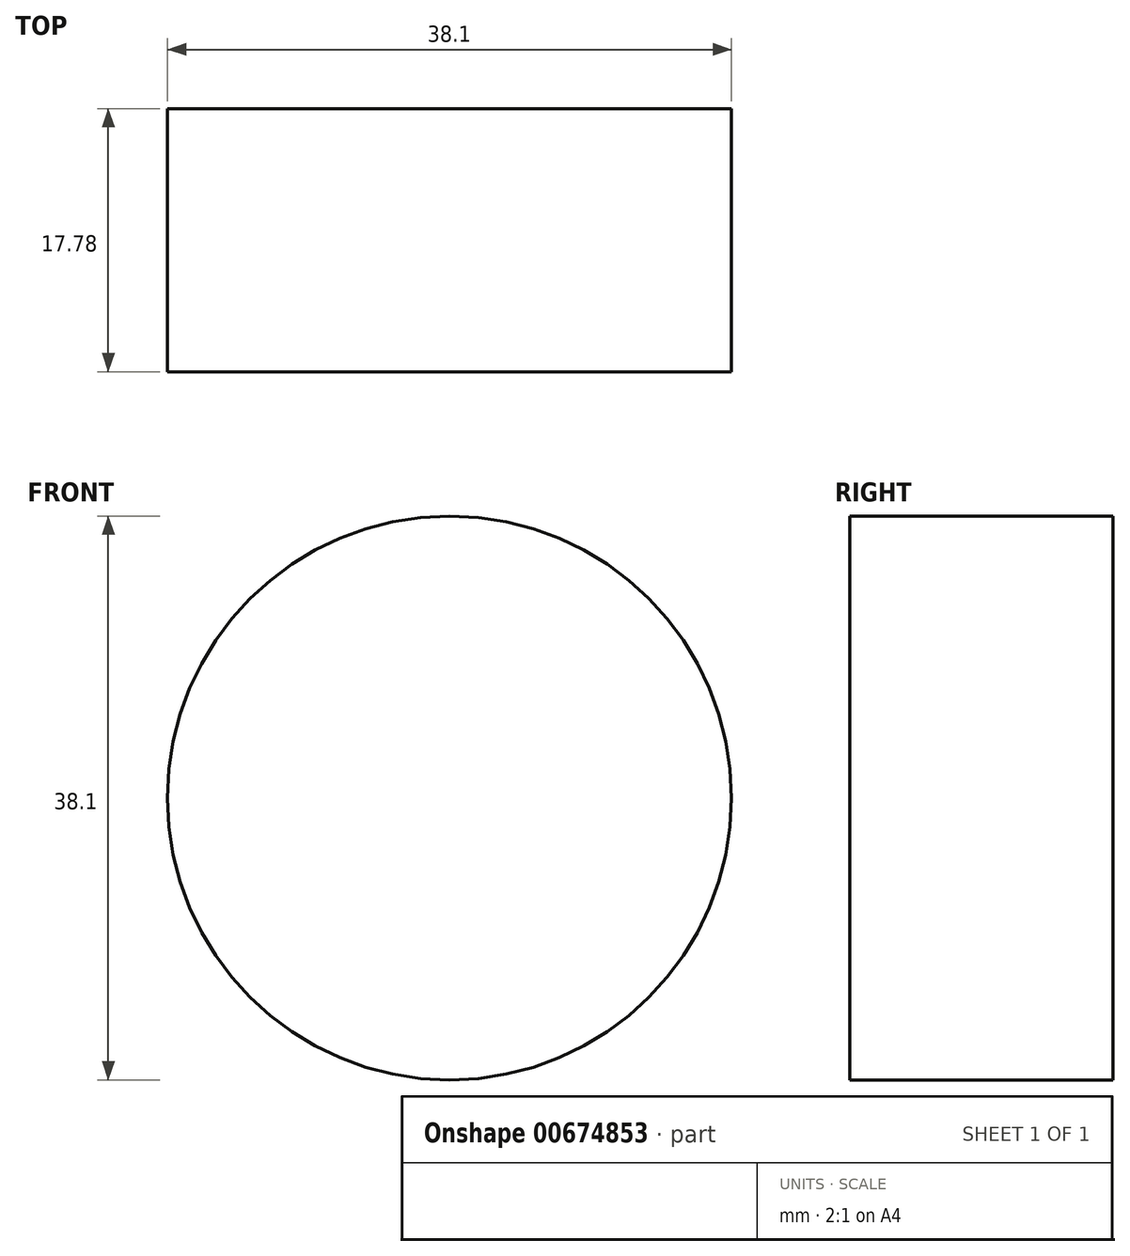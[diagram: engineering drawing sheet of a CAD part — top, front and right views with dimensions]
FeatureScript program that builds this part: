
annotation { "Feature Type Name" : "Feature", "Feature Type Description" : "" }
export const myFeature = defineFeature(function(context is Context, id is Id, definition is map)
    precondition{}
    {
        {
            var Q0;
            Q0=qCreatedBy(makeId("Front.planeOp"),FACE);
            var sketch = newSketch(context, id + "F0", { "sketchPlane" : qUnion([Q0])});
            skCircle(sketch, "E0", {"center": v(-37.42, 0) * mm, "radius": 19.05 * mm});
            skSolve(sketch);
        }
        {
            var Q0;
            Q0=makeQuery(id+"F0.imprint","IMPRINT",FACE,{"disambiguationData":[TD([[makeQuery(id+"F0.imprint","IMPRINT",EDGE,{"derivedFrom":sQuery(id+"F0.wireOp",EDGE,"E0")}),1.0]])]});
            extrude(context, id + "F1", {"entities" : qUnion([Q0]), "oppositeDirection" : true, "depth" : 17.78 * mm, "offsetDistance" : 25.4 * mm});
        }
    });
